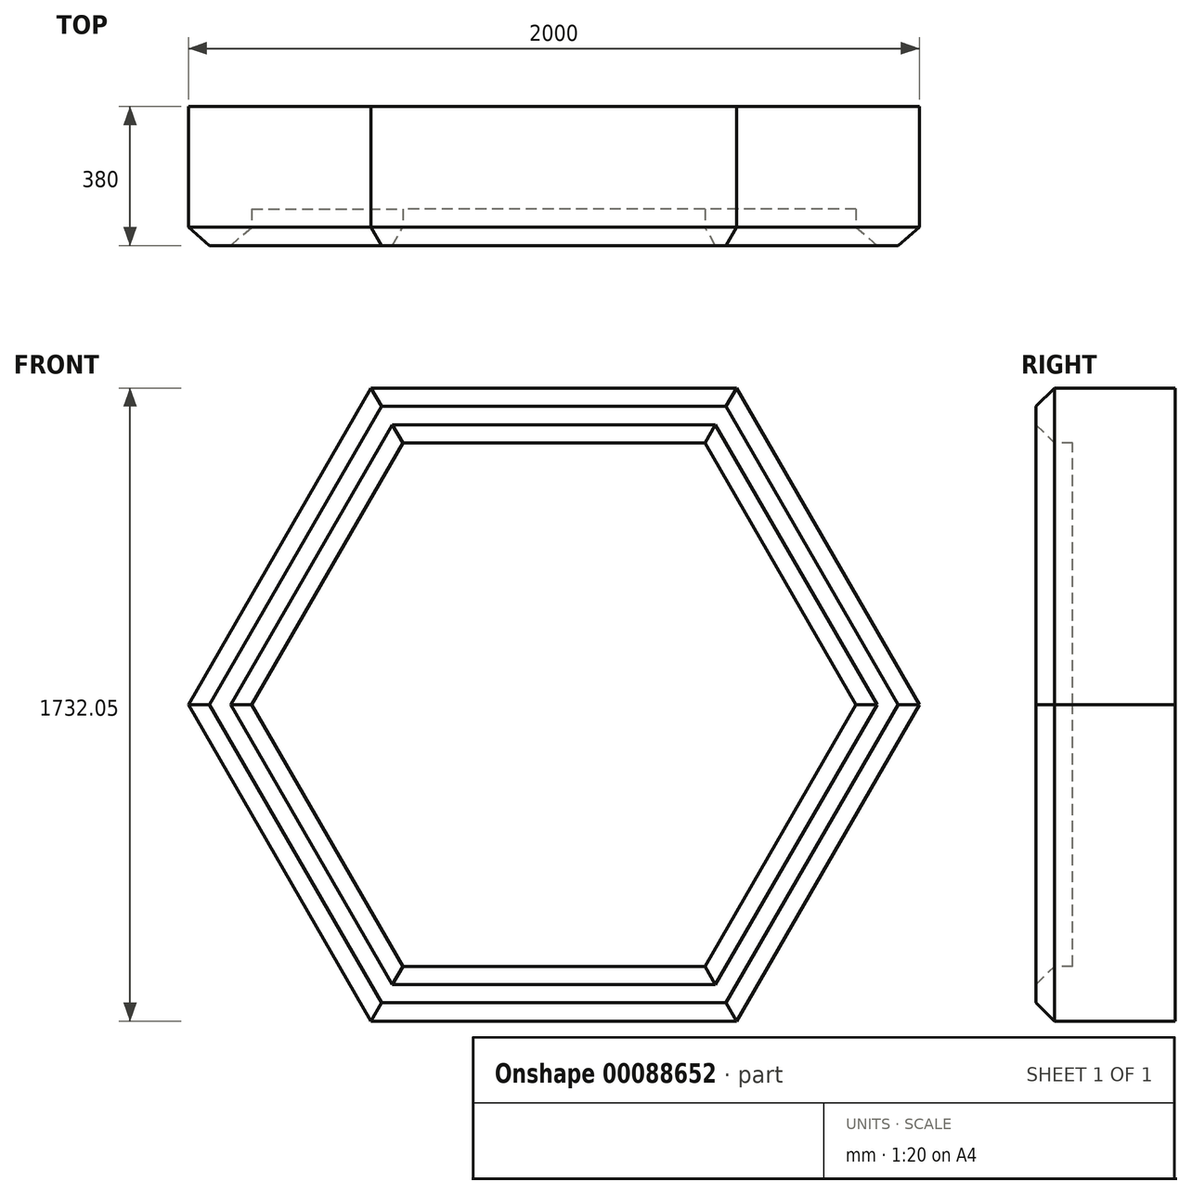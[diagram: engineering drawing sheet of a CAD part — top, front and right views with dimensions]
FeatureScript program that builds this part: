
annotation { "Feature Type Name" : "Feature", "Feature Type Description" : "" }
export const myFeature = defineFeature(function(context is Context, id is Id, definition is map)
    precondition{}
    {
        {
            var Q0;
            Q0=qCreatedBy(makeId("Top.planeOp"),FACE);
            var sketch = newSketch(context, id + "F0", { "sketchPlane" : qUnion([Q0])});
            skCircle(sketch, "E0.cCircle", {"center": v(0, 0) * mm, "radius": 866.03 * mm, "construction": true});
            skLineSegment(sketch, "E0.0", {"start": v(-500, 866.03) * mm, "end": v(500, 866.03) * mm});
            skLineSegment(sketch, "E0.1", {"start": v(500, 866.03) * mm, "end": v(1000, 0) * mm});
            skLineSegment(sketch, "E0.2", {"start": v(1000, 0) * mm, "end": v(500, -866.03) * mm});
            skLineSegment(sketch, "E0.3", {"start": v(500, -866.03) * mm, "end": v(-500, -866.03) * mm});
            skLineSegment(sketch, "E0.4", {"start": v(-500, -866.03) * mm, "end": v(-1000, 0) * mm});
            skLineSegment(sketch, "E0.5", {"start": v(-1000, 0) * mm, "end": v(-500, 866.03) * mm});
            skPoint(sketch, "E0.0.midPoint", {"position": v(0, 866.03) * mm});
            skSolve(sketch);
        }
        {
            var Q0;
            Q0=makeQuery(id+"F0.imprint","IMPRINT",FACE,{"disambiguationData":[TD([[makeQuery(id+"F0.imprint","IMPRINT",EDGE,{"derivedFrom":sQuery(id+"F0.wireOp",EDGE,"E0.0")}),-1.0]])]});
            extrude(context, id + "F1", {"entities" : qUnion([Q0]), "depth" : 380 * mm});
        }
        {
            var Q0;
            Q0=makeQuery(id+"F1.opExtrude","CAP_FACE",FACE,{"disambiguationData":[OSD([sQuery(id+"F0.wireOp",EDGE,"E0.0"),sQuery(id+"F0.wireOp",EDGE,"E0.1"),sQuery(id+"F0.wireOp",EDGE,"E0.2"),sQuery(id+"F0.wireOp",EDGE,"E0.3"),sQuery(id+"F0.wireOp",EDGE,"E0.4"),sQuery(id+"F0.wireOp",EDGE,"E0.5")])],"isStart":false});
            var sketch = newSketch(context, id + "F2", { "sketchPlane" : qUnion([Q0])});
            skLineSegment(sketch, "E1.0", {"start": v(-413.4, -716.03) * mm, "end": v(-826.8, 0) * mm});
            skLineSegment(sketch, "E1.1", {"start": v(-413.4, 716.03) * mm, "end": v(413.4, 716.03) * mm});
            skLineSegment(sketch, "E1.2", {"start": v(413.4, 716.03) * mm, "end": v(826.8, 0) * mm});
            skLineSegment(sketch, "E1.3", {"start": v(-826.8, 0) * mm, "end": v(-413.4, 716.03) * mm});
            skLineSegment(sketch, "E1.4", {"start": v(826.8, 0) * mm, "end": v(413.4, -716.03) * mm});
            skLineSegment(sketch, "E1.5", {"start": v(413.4, -716.03) * mm, "end": v(-413.4, -716.03) * mm});
            skLineSegment(sketch, "E2.0", {"start": v(994.23, 0) * mm, "end": v(497.11, 861.03) * mm});
            skLineSegment(sketch, "E2.1", {"start": v(-497.11, 861.03) * mm, "end": v(-994.23, 0) * mm});
            skLineSegment(sketch, "E2.2", {"start": v(-994.23, 0) * mm, "end": v(-497.11, -861.03) * mm});
            skLineSegment(sketch, "E2.3", {"start": v(497.11, 861.03) * mm, "end": v(-497.11, 861.03) * mm});
            skLineSegment(sketch, "E2.4", {"start": v(-497.11, -861.03) * mm, "end": v(497.11, -861.03) * mm});
            skLineSegment(sketch, "E2.5", {"start": v(497.11, -861.03) * mm, "end": v(994.23, 0) * mm});
            skSolve(sketch);
        }
        {
            var Q0;
            Q0=makeQuery(id+"F2.imprint","IMPRINT",FACE,{"disambiguationData":[TD([[makeQuery(id+"F2.imprint","IMPRINT",EDGE,{"derivedFrom":sQuery(id+"F2.wireOp",EDGE,"E1.0")}),-1.0]])]});
            extrude(context, id + "F3", {"entities" : qUnion([Q0]), "operationType" : NewBodyOperationType.REMOVE, "oppositeDirection" : true, "depth" : 100 * mm});
        }
        {
            var Q0;
            Q0=makeQuery(id+"F1.opExtrude","CAP_FACE",FACE,{"disambiguationData":[OSD([sQuery(id+"F0.wireOp",EDGE,"E0.0"),sQuery(id+"F0.wireOp",EDGE,"E0.1"),sQuery(id+"F0.wireOp",EDGE,"E0.2"),sQuery(id+"F0.wireOp",EDGE,"E0.3"),sQuery(id+"F0.wireOp",EDGE,"E0.4"),sQuery(id+"F0.wireOp",EDGE,"E0.5")])],"isStart":false});
            chamfer(context, id + "F4", {"entities" : qUnion([Q0]), "width" : 50 * mm, "tangentPropagation" : true});
        }
        {
            var Q0;
            Q0=makeQuery(id+"F1.opExtrude","SWEPT_BODY",BODY,{"disambiguationData":[OSD([sQuery(id+"F0.wireOp",EDGE,"E0.0"),sQuery(id+"F0.wireOp",EDGE,"E0.1"),sQuery(id+"F0.wireOp",EDGE,"E0.2"),sQuery(id+"F0.wireOp",EDGE,"E0.3"),sQuery(id+"F0.wireOp",EDGE,"E0.4"),sQuery(id+"F0.wireOp",EDGE,"E0.5")])]});
            var Q1;
            Q1=makeQuery(id+"F1.opExtrude","CAP_EDGE",EDGE,{"disambiguationData":[OSD([sQuery(id+"F0.wireOp",EDGE,"E0.3")])],"isStart":true});
            transform(context, id + "F5", {"entities" : qUnion([Q0]), "transformType" : TransformType.ROTATION, "transformAxis" : qUnion([Q1]), "angle" : 90 * degree, "oppositeDirection" : true, "makeCopy" : false});
        }
    });
